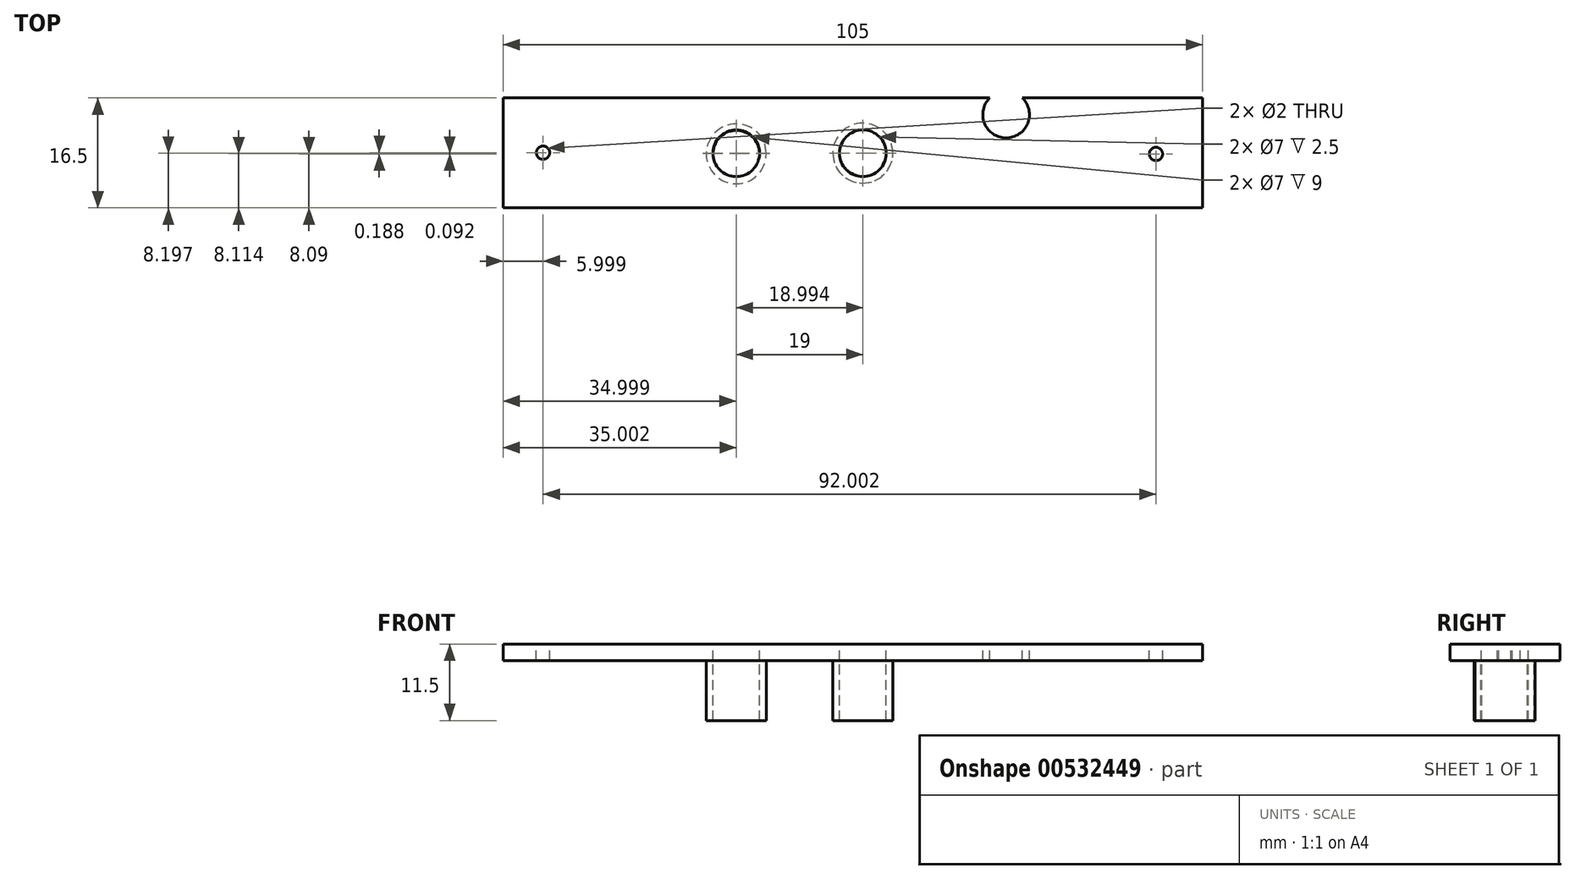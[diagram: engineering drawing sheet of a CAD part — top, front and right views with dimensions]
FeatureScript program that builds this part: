
annotation { "Feature Type Name" : "Feature", "Feature Type Description" : "" }
export const myFeature = defineFeature(function(context is Context, id is Id, definition is map)
    precondition{}
    {
        {
            var Q0;
            Q0=qCreatedBy(makeId("Top.planeOp"),FACE);
            var sketch = newSketch(context, id + "F0", { "sketchPlane" : qUnion([Q0])});
            skLineSegment(sketch, "E0", {"start": v(-39.6, 24.39) * mm, "end": v(65.4, 24.39) * mm});
            skLineSegment(sketch, "E1", {"start": v(65.4, 24.39) * mm, "end": v(65.4, 7.89) * mm});
            skLineSegment(sketch, "E2", {"start": v(65.4, 7.89) * mm, "end": v(-39.6, 7.89) * mm});
            skLineSegment(sketch, "E3", {"start": v(-39.6, 7.89) * mm, "end": v(-39.6, 24.39) * mm});
            skSolve(sketch);
        }
        {
            var Q0;
            Q0 = qSketchRegion(id + "F0", true);
            extrude(context, id + "F1", {"entities" : qUnion([Q0]), "oppositeDirection" : true, "depth" : 2.5 * mm, "offsetDistance" : 25 * mm});
        }
        {
            var Q0;
            Q0=makeQuery(id+"F1.opExtrude","CAP_FACE",FACE,{"disambiguationData":[OSD([sQuery(id+"F0.wireOp",EDGE,"E0"),sQuery(id+"F0.wireOp",EDGE,"E1"),sQuery(id+"F0.wireOp",EDGE,"E2"),sQuery(id+"F0.wireOp",EDGE,"E3")])],"isStart":true});
            var sketch = newSketch(context, id + "F2", { "sketchPlane" : qUnion([Q0])});
            skCircle(sketch, "E4", {"center": v(35.9, 21.89) * mm, "radius": 3.5 * mm});
            skCircle(sketch, "E5", {"center": v(-4.6, 16.09) * mm, "radius": 3.5 * mm});
            skCircle(sketch, "E6", {"center": v(14.4, 16.09) * mm, "radius": 3.5 * mm});
            skCircle(sketch, "E7", {"center": v(-33.6, 16.17) * mm, "radius": 1 * mm});
            skCircle(sketch, "E8", {"center": v(58.4, 15.98) * mm, "radius": 1 * mm});
            skSolve(sketch);
        }
        {
            var Q0;
            {var subQ0=sQuery(id+"F2.wireOp",EDGE,"E4");var subQ1=makeQuery(id+"F1.opExtrude","CAP_EDGE",EDGE,{"disambiguationData":[OSD([sQuery(id+"F0.wireOp",EDGE,"E0")])],"isStart":true});var subQ2=makeQuery(id+"F2.imprint","INTERSECT",VERTEX,{"disambiguationData":[OD(0.0)],"derivedFrom":[subQ1,subQ0]});Q0=makeQuery(id+"F2.imprint","IMPRINT",FACE,{"disambiguationData":[TD([[makeQuery(id+"F2.imprint","IMPRINT",EDGE,{"disambiguationData":[TD([[subQ2,-1.0]])],"derivedFrom":subQ0}),1.0]])]});}
            var Q1;
            Q1=makeQuery(id+"F2.imprint","IMPRINT",FACE,{"disambiguationData":[TD([[makeQuery(id+"F2.imprint","IMPRINT",EDGE,{"derivedFrom":sQuery(id+"F2.wireOp",EDGE,"E5")}),1.0]])]});
            var Q2;
            Q2=makeQuery(id+"F2.imprint","IMPRINT",FACE,{"disambiguationData":[TD([[makeQuery(id+"F2.imprint","IMPRINT",EDGE,{"derivedFrom":sQuery(id+"F2.wireOp",EDGE,"E6")}),1.0]])]});
            var Q3;
            Q3=makeQuery(id+"F1.opExtrude","CAP_FACE",FACE,{"disambiguationData":[OSD([sQuery(id+"F0.wireOp",EDGE,"E0"),sQuery(id+"F0.wireOp",EDGE,"E1"),sQuery(id+"F0.wireOp",EDGE,"E2"),sQuery(id+"F0.wireOp",EDGE,"E3")])],"isStart":false});
            var Q4;
            Q4=makeQuery(id+"F2.imprint","IMPRINT",FACE,{"disambiguationData":[TD([[makeQuery(id+"F2.imprint","IMPRINT",EDGE,{"derivedFrom":sQuery(id+"F2.wireOp",EDGE,"E7")}),1.0]])]});
            var Q5;
            Q5=makeQuery(id+"F2.imprint","IMPRINT",FACE,{"disambiguationData":[TD([[makeQuery(id+"F2.imprint","IMPRINT",EDGE,{"derivedFrom":sQuery(id+"F2.wireOp",EDGE,"E8")}),1.0]])]});
            extrude(context, id + "F3", {"entities" : qUnion([Q0, Q1, Q2, Q3, Q4, Q5]), "operationType" : NewBodyOperationType.REMOVE, "oppositeDirection" : true, "depth" : 2.5 * mm, "offsetDistance" : 25 * mm});
        }
        {
            var Q0;
            Q0=makeQuery(id+"F1.opExtrude","CAP_FACE",FACE,{"disambiguationData":[OSD([sQuery(id+"F0.wireOp",EDGE,"E0"),sQuery(id+"F0.wireOp",EDGE,"E1"),sQuery(id+"F0.wireOp",EDGE,"E2"),sQuery(id+"F0.wireOp",EDGE,"E3")])],"isStart":false});
            var sketch = newSketch(context, id + "F4", { "sketchPlane" : qUnion([Q0])});
            skPoint(sketch, "E9.centerSnap0", {"position": v(-39.6, -16.14) * mm});
            skSolve(sketch);
        }
        {
            var Q0;
            {var subQ2=sQuery(id+"F0.wireOp",EDGE,"E1");Q0=makeQuery(id+"F4.imprint","IMPRINT",FACE,{"disambiguationData":[TD([[makeQuery(id+"F4.imprint","IMPRINT",EDGE,{"derivedFrom":makeQuery(id+"F1.opExtrude","CAP_EDGE",EDGE,{"disambiguationData":[OSD([subQ2])],"isStart":false})}),1.0]])]});}
            var sketch = newSketch(context, id + "F5", { "sketchPlane" : qUnion([Q0])});
            skCircle(sketch, "E10", {"center": v(-4.6, -16) * mm, "radius": 4.5 * mm});
            skCircle(sketch, "E11", {"center": v(-4.6, -16) * mm, "radius": 3.5 * mm});
            skCircle(sketch, "E12", {"center": v(14.4, -16.1) * mm, "radius": 3.5 * mm});
            skCircle(sketch, "E13", {"center": v(14.4, -16.1) * mm, "radius": 4.5 * mm});
            skSolve(sketch);
        }
        {
            var Q0;
            Q0 = qSketchRegion(id + "F5", true);
            extrude(context, id + "F6", {"entities" : qUnion([Q0]), "operationType" : NewBodyOperationType.ADD, "depth" : 9 * mm, "offsetDistance" : 25 * mm});
        }
        {
            var Q0;
            Q0 = qSketchRegion(id + "F5", true);
            extrude(context, id + "F7", {"entities" : qUnion([Q0]), "operationType" : NewBodyOperationType.ADD, "depth" : 9 * mm, "offsetDistance" : 25 * mm});
        }
    });
